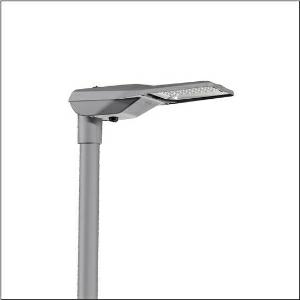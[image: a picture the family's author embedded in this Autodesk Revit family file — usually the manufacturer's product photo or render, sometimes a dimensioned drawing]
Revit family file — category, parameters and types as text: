
# Revit family: streetlight_sl_21_mini___st0_8a_5xe2c43t08gb_5b97
name_source: partatom
category: Lighting Fixtures
units: mm (PartAtom-declared; Revit-internal decimal feet)

## family parameters
Cut with Voids When Loaded = No
Host = Face
Light Source = No
Part Type = Normal
Room Calculation Point = No
Round Connector Dimension = Use Diameter
Shared = No

## types (1)
- --- (1 x LED, 6180 lm, 40.4 W, 4000K)
    Apparent Load = 40 VA
    CIE Flux Codes = 38 75 97 100 100
    Color Rendering = 70
    Color Temperature = 4000K
    Default Elevation = 1800 mm
    Description = Streetlight SL 21 mini, mast luminaire, primary light control with lens, of PMMA, primary optical cover: cover, of toughened safety glass, transparent, light distribution: ST0.8a, light emission: direct distribution, primary light characteristic: asymmetric, installation type: side-entry, post-top, LED, High Power LED, rated luminous flux: 6.180lm, luminous efficacy: 153lm/W, light colour: 740, colour temperature: 4000K, control gear: D4i, control: overheat protection, constant luminous flux control, time-dependent luminous flux control, flexible luminous flux parameterisation, pre-setting: logarithmic dimming characteristic, mains connection: 220..240V, AC, 50/60Hz, start of lifetime: 40W, end of service life: 41W, reduction: 19W, luminaire housing, of diecast aluminium, powder-coated, Siteco® metallic grey (DB 702S), corrosivity category C5 mid according to DIN EN ISO 12944, please order mast flange separately, inclination adjustable: 0°, 5°, 10°, 15°, sealing non-destructively replaceable, multi-level sealing system, length: 628mm, width: 235mm, height: 110mm, mast flange for spigot size: 42mm (side-entry): 5XC10008XM4, 60/48mm (side-entry/post-top): 5XC10108XM2, 76/60mm (side-entry/post-top): 5XC10108XM1, mounting height: 4..8m, Smart Interface below and above, protection rating (complete): IP66, insulation class (complete): insulation class II (safety insulation), certification: CE, ENEC, ENEC+, VDE, impact resistance: IK10, permissible operating ambient temperature for outdoor applications: -40..+50°C, standard-compliant lighting for roads and squares, packaging unit: 1 piece

Light Distribution: ST0.8a
    Height = 110 mm
    Lamp = 1 x LED
    Lamp Light Flux = 6180 lm
    Lamp Power = 40.4 W
    Lamp count = 1
    Length = 625 mm
    Luminous efficacy = 153 lm/W
    Manufacturer = Siteco
    ModVariant = No
    Model = 5XE2C43T08GB
    Number of Poles = 1
    OnlyDefault = Yes
    Power Factor = 1
    Product Name = Streetlight SL 21 mini | ST0.8a
    Product group = mast luminaire | pylon top
    ProductGroupID = 6100
    Protection Class = Protection class II
    Protection Degree = IP 66
    RLX_Detail_Level = 1
    RLX_Emergency_Light_Flux = 0 lm
    RLX_Emergency_Type = 0
    RLX_Emergency_Type_DB = No
    RlxData = <blob elided: 26405 chars, md5=c24c3163>
    Socket = socket
    Standby Power = 0 W
    System Light Flux = 6180 lm
    System Power = 40 W
    Type Comments = factory setting: luminous flux: 100 % | dim-lin: 254 | 812 mA
    Type Image = l_1003514.jpg
    URL = http://relux.com
    VarID = @adj_206679
    Voltage = 0 V
    Weight = 0.00 kg
    Width = 234 mm

## geometry (parser evidence)
native form markers: Blend x4, Sweep x12
no freeform markers — native parametric forms only
